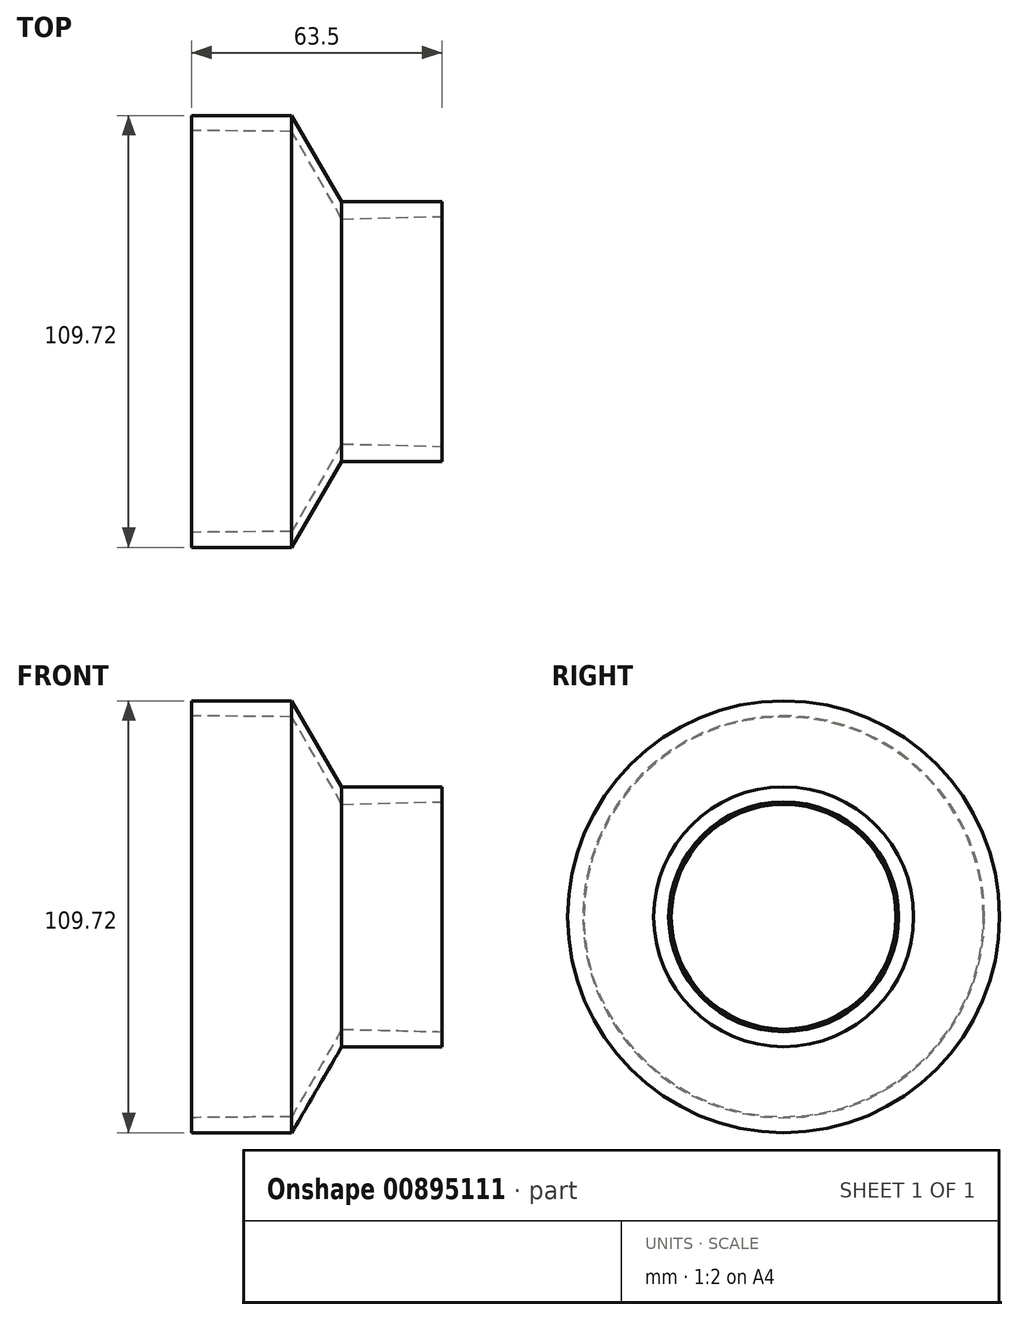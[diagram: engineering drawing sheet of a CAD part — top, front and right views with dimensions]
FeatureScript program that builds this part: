
annotation { "Feature Type Name" : "Feature", "Feature Type Description" : "" }
export const myFeature = defineFeature(function(context is Context, id is Id, definition is map)
    precondition{}
    {
        {
            var Q0;
            Q0=qCreatedBy(makeId("Front.planeOp"),FACE);
            var sketch = newSketch(context, id + "F0", { "sketchPlane" : qUnion([Q0])});
            skLineSegment(sketch, "E0", {"start": v(0, 0) * mm, "end": v(-90.9, 0) * mm, "construction": true});
            skLineSegment(sketch, "E1", {"start": v(0, 33.02) * mm, "end": v(25.4, 33.02) * mm});
            skLineSegment(sketch, "E2", {"start": v(25.4, 33.02) * mm, "end": v(25.4, 29.21) * mm});
            skLineSegment(sketch, "E3", {"start": v(25.4, 29.21) * mm, "end": v(0, 28.58) * mm});
            skLineSegment(sketch, "E4", {"start": v(0, 28.58) * mm, "end": v(-12.7, 50.8) * mm});
            skLineSegment(sketch, "E5", {"start": v(-12.7, 50.8) * mm, "end": v(-38.1, 51.05) * mm});
            skLineSegment(sketch, "E6", {"start": v(-38.1, 51.05) * mm, "end": v(-38.1, 54.86) * mm});
            skLineSegment(sketch, "E7", {"start": v(-38.1, 54.86) * mm, "end": v(-12.7, 54.86) * mm});
            skLineSegment(sketch, "E8", {"start": v(-12.7, 54.86) * mm, "end": v(0, 33.02) * mm});
            skPoint(sketch, "E9", {"position": v(0, 28.58) * mm});
            skPoint(sketch, "E10", {"position": v(-12.7, 50.8) * mm});
            skLineSegment(sketch, "E11", {"start": v(-12.7, 50.8) * mm, "end": v(-12.7, 54.86) * mm, "construction": true});
            skSolve(sketch);
        }
        {
            var Q0;
            Q0=qSketchRegion(id+"F0",true);
            var Q1;
            Q1=sQuery(id+"F0.wireOp",EDGE,"E0");
            revolve(context, id + "F1", {"surfaceOperationType" : NewSurfaceOperationType.NEW, "entities" : qUnion([Q0]), "axis" : qUnion([Q1]), "revolveType" : RevolveType.FULL});
        }
    });
